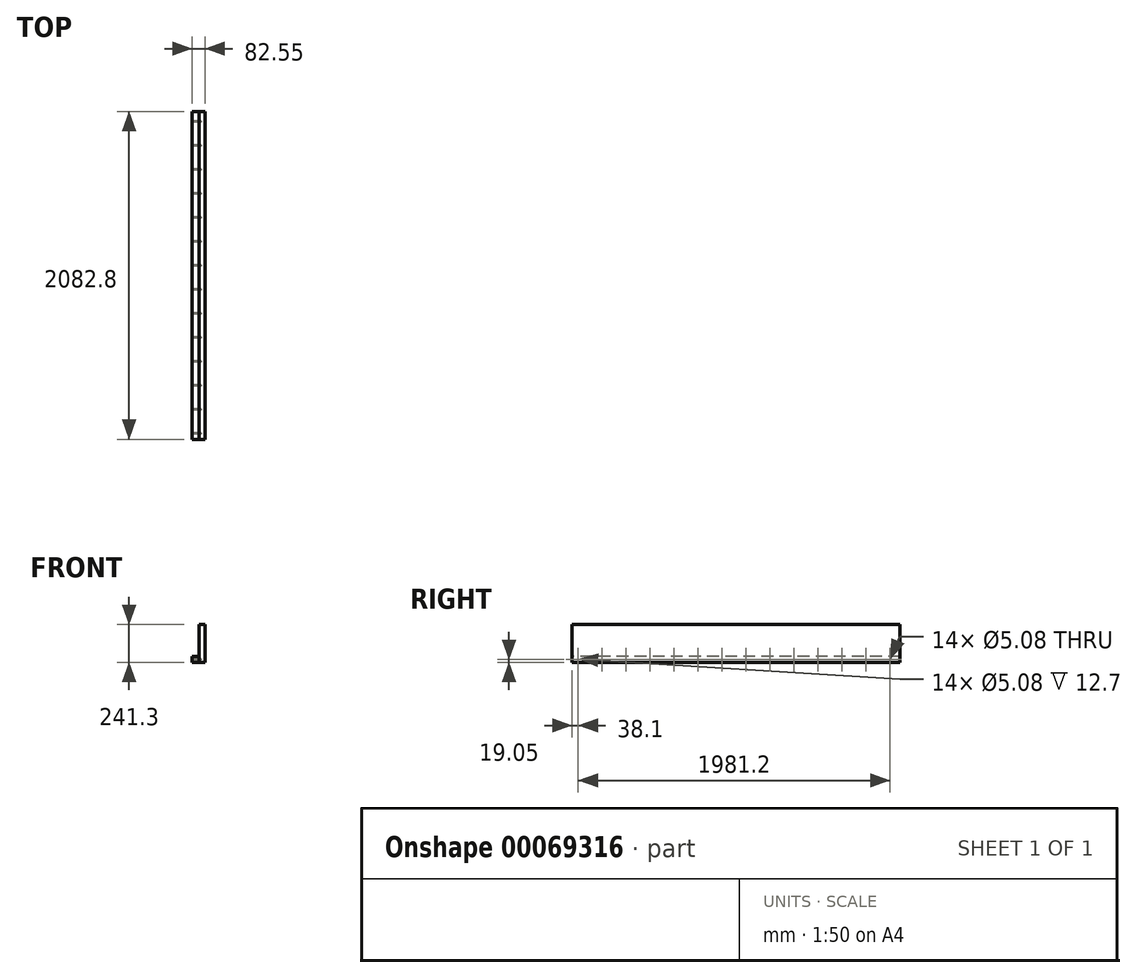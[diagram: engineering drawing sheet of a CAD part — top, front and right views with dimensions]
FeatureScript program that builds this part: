
annotation { "Feature Type Name" : "Feature", "Feature Type Description" : "" }
export const myFeature = defineFeature(function(context is Context, id is Id, definition is map)
    precondition{}
    {
        {
            var Q0;
            Q0=qCreatedBy(makeId("Right.planeOp"),FACE);
            var sketch = newSketch(context, id + "F0", { "sketchPlane" : qUnion([Q0])});
            skLineSegment(sketch, "E0.rect.bottom", {"start": v(-1041.4, 120.65) * mm, "end": v(1041.4, 120.65) * mm});
            skLineSegment(sketch, "E0.rect.top", {"start": v(-1041.4, -120.65) * mm, "end": v(1041.4, -120.65) * mm});
            skLineSegment(sketch, "E0.rect.left", {"start": v(-1041.4, 120.65) * mm, "end": v(-1041.4, -120.65) * mm});
            skLineSegment(sketch, "E0.rect.right", {"start": v(1041.4, 120.65) * mm, "end": v(1041.4, -120.65) * mm});
            skPoint(sketch, "E0.rect.middle", {"position": v(0, 0) * mm});
            skSolve(sketch);
        }
        {
            var Q0;
            Q0 = qSketchRegion(id + "F0", true);
            extrude(context, id + "F1", {"entities" : qUnion([Q0]), "depth" : 38.1 * mm});
        }
        {
            var Q0;
            Q0=makeQuery(id+"F1.opExtrude","CAP_FACE",FACE,{"disambiguationData":[OSD([sQuery(id+"F0.wireOp",EDGE,"E0.rect.bottom"),sQuery(id+"F0.wireOp",EDGE,"E0.rect.top"),sQuery(id+"F0.wireOp",EDGE,"E0.rect.left"),sQuery(id+"F0.wireOp",EDGE,"E0.rect.right")])],"isStart":true});
            var sketch = newSketch(context, id + "F2", { "sketchPlane" : qUnion([Q0])});
            skLineSegment(sketch, "E1.bottom", {"start": v(-1041.4, -82.55) * mm, "end": v(1041.4, -82.55) * mm});
            skLineSegment(sketch, "E1.top", {"start": v(-1041.4, -120.65) * mm, "end": v(1041.4, -120.65) * mm});
            skLineSegment(sketch, "E1.left", {"start": v(-1041.4, -82.55) * mm, "end": v(-1041.4, -120.65) * mm});
            skLineSegment(sketch, "E1.right", {"start": v(1041.4, -82.55) * mm, "end": v(1041.4, -120.65) * mm});
            skSolve(sketch);
        }
        {
            var Q0;
            Q0 = qSketchRegion(id + "F2", true);
            extrude(context, id + "F3", {"entities" : qUnion([Q0]), "depth" : 44.45 * mm});
        }
        {
            var Q0;
            Q0=makeQuery(id+"F3.opExtrude","CAP_FACE",FACE,{"disambiguationData":[OSD([sQuery(id+"F2.wireOp",EDGE,"E1.bottom"),sQuery(id+"F2.wireOp",EDGE,"E1.top"),sQuery(id+"F2.wireOp",EDGE,"E1.left"),sQuery(id+"F2.wireOp",EDGE,"E1.right")])],"isStart":false});
            var sketch = newSketch(context, id + "F4", { "sketchPlane" : qUnion([Q0])});
            skCircle(sketch, "E2", {"center": v(1003.3, -101.6) * mm, "radius": 2.54 * mm});
            skLineSegment(sketch, "E3", {"start": v(1041.4, -101.6) * mm, "end": v(1003.3, -101.6) * mm, "construction": true});
            skCircle(sketch, "E4.1.0.0", {"center": v(850.9, -101.6) * mm, "radius": 2.54 * mm});
            skCircle(sketch, "E4.2.0.0", {"center": v(698.5, -101.6) * mm, "radius": 2.54 * mm});
            skCircle(sketch, "E4.3.0.0", {"center": v(546.1, -101.6) * mm, "radius": 2.54 * mm});
            skCircle(sketch, "E4.4.0.0", {"center": v(393.7, -101.6) * mm, "radius": 2.54 * mm});
            skCircle(sketch, "E4.5.0.0", {"center": v(241.3, -101.6) * mm, "radius": 2.54 * mm});
            skCircle(sketch, "E4.6.0.0", {"center": v(88.9, -101.6) * mm, "radius": 2.54 * mm});
            skCircle(sketch, "E4.7.0.0", {"center": v(-63.5, -101.6) * mm, "radius": 2.54 * mm});
            skCircle(sketch, "E4.8.0.0", {"center": v(-215.9, -101.6) * mm, "radius": 2.54 * mm});
            skCircle(sketch, "E4.9.0.0", {"center": v(-368.3, -101.6) * mm, "radius": 2.54 * mm});
            skCircle(sketch, "E4.10.0.0", {"center": v(-520.7, -101.6) * mm, "radius": 2.54 * mm});
            skCircle(sketch, "E4.11.0.0", {"center": v(-673.1, -101.6) * mm, "radius": 2.54 * mm});
            skCircle(sketch, "E4.12.0.0", {"center": v(-825.5, -101.6) * mm, "radius": 2.54 * mm});
            skCircle(sketch, "E4.13.0.0", {"center": v(-977.9, -101.6) * mm, "radius": 2.54 * mm});
            skLineSegment(sketch, "E4.direction1", {"start": v(1003.3, -101.6) * mm, "end": v(850.9, -101.6) * mm, "construction": true});
            skSolve(sketch);
        }
        {
            var Q0;
            Q0 = qSketchRegion(id + "F4", true);
            extrude(context, id + "F5", {"entities" : qUnion([Q0]), "operationType" : NewBodyOperationType.REMOVE, "oppositeDirection" : true, "depth" : 57.15 * mm});
        }
    });
